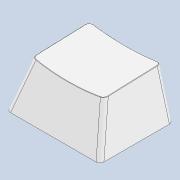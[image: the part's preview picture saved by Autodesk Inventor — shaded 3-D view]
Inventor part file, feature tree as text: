
AUTODESK INVENTOR PART (.ipt)
format: ipt  version: 2021 (Build 250183000, 183)  size: 246,272 bytes
history: native  units: in
note: dims shown in document units (in); Inventor stores cm internally (conversion verified against a paired STEP export)
features: chamfer x1
ambient origin geometry x8: Origin, YZ Plane, XZ Plane, XY Plane, X Axis, Y Axis, Z Axis, Center Point
bodies: Solid1 (feature_tree)
feature tree (1):
  chamfer  "Chamfer1"  [1 undecoded]
note: 1 required parameter value undecoded (feature->parameter linkage not recoverable at this tier; creation-order binding heuristic only, values carry confidence <= 0.55)
